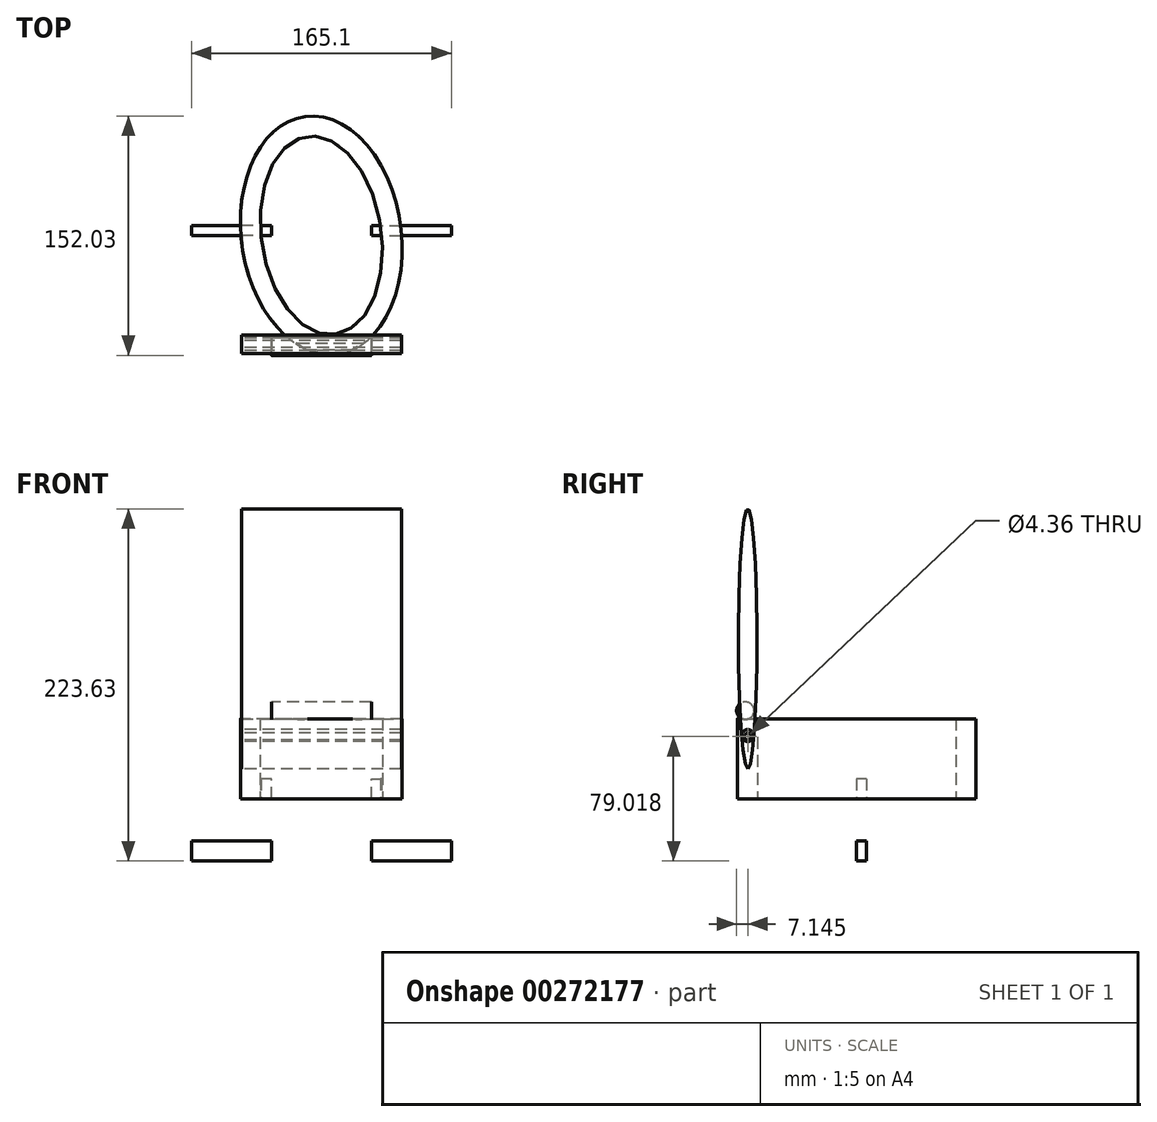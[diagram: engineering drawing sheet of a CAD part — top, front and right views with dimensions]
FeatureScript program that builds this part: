
annotation { "Feature Type Name" : "Feature", "Feature Type Description" : "" }
export const myFeature = defineFeature(function(context is Context, id is Id, definition is map)
    precondition{}
    {
        {
            var Q0;
            Q0=qCreatedBy(makeId("Top.planeOp"),FACE);
            var sketch = newSketch(context, id + "F0", { "sketchPlane" : qUnion([Q0])});
            skEllipse(sketch, "E0", {"center": v(0, 0) * mm, "majorRadius": 76.2 * mm, "minorRadius": 50.8 * mm, "majorAxis": v(-0.14, 1)});
            skEllipse(sketch, "E1", {"center": v(0, 0) * mm, "majorRadius": 63.5 * mm, "minorRadius": 38.1 * mm, "majorAxis": v(0.14, -0.99)});
            skSolve(sketch);
        }
        {
            var Q0;
            Q0 = qSketchRegion(id + "F0", true);
            extrude(context, id + "F1", {"entities" : qUnion([Q0]), "depth" : 50.8 * mm});
        }
        {
            var Q0;
            Q0=qCreatedBy(makeId("Right.planeOp"),FACE);
            var sketch = newSketch(context, id + "F2", { "sketchPlane" : qUnion([Q0])});
            skCircle(sketch, "E2", {"center": v(-70.68, 55.96) * mm, "radius": 5.55 * mm});
            skPoint(sketch, "E2.first.point", {"position": v(-69.37, 50.57) * mm});
            skPoint(sketch, "E2.second.point", {"position": v(-76.08, 57.27) * mm});
            skPoint(sketch, "E2.third.point", {"position": v(-65.58, 58.15) * mm});
            skSolve(sketch);
        }
        {
            var Q0;
            Q0 = qSketchRegion(id + "F2", true);
            extrude(context, id + "F3", {"entities" : qUnion([Q0]), "operationType" : NewBodyOperationType.ADD, "endBound" : BoundingType.SYMMETRIC, "depth" : 63.5 * mm});
        }
        {
            var Q0;
            Q0=qCreatedBy(makeId("Right.planeOp"),FACE);
            var sketch = newSketch(context, id + "F4", { "sketchPlane" : qUnion([Q0])});
            skLineSegment(sketch, "E3", {"start": v(-75.48, 50.8) * mm, "end": v(-75.48, 101.6) * mm});
            skLineSegment(sketch, "E4", {"start": v(-75.48, 101.6) * mm, "end": v(-69.13, 101.6) * mm});
            skEllipse(sketch, "E5", {"center": v(-69.13, 101.6) * mm, "majorRadius": 82.55 * mm, "minorRadius": 5.9 * mm, "majorAxis": v(0, -1)});
            skCircle(sketch, "E6", {"center": v(-69.09, 39.54) * mm, "radius": 2.18 * mm});
            skPoint(sketch, "E7", {"position": v(-66.83, 25.61) * mm});
            skPoint(sketch, "E8", {"position": v(-71.43, 25.61) * mm});
            skPoint(sketch, "E9", {"position": v(-69.09, 19.06) * mm});
            skPoint(sketch, "E10", {"position": v(-69.42, 66.59) * mm});
            skPoint(sketch, "E11", {"position": v(-69.42, 55.14) * mm});
            skPoint(sketch, "E12", {"position": v(-72.52, 34.04) * mm});
            skPoint(sketch, "E13", {"position": v(-76.14, 43.42) * mm});
            skPoint(sketch, "E14", {"position": v(-73.53, 46.73) * mm});
            skPoint(sketch, "E15", {"position": v(-79.04, 51.6) * mm});
            skPoint(sketch, "E16", {"position": v(-79.04, 59) * mm});
            skPoint(sketch, "E17", {"position": v(-93.58, 72.66) * mm});
            skPoint(sketch, "E18", {"position": v(-114.57, 57.23) * mm});
            skPoint(sketch, "E19", {"position": v(-122, 80.72) * mm});
            skPoint(sketch, "E20", {"position": v(-131.05, 64.73) * mm});
            skPoint(sketch, "E21", {"position": v(-91.64, 41.1) * mm});
            skPoint(sketch, "E22", {"position": v(-123.62, 70.9) * mm});
            skPoint(sketch, "E23", {"position": v(-112.64, 63.73) * mm});
            skPoint(sketch, "E24", {"position": v(-153.33, 104.96) * mm});
            skPoint(sketch, "E25", {"position": v(-150.43, 97.35) * mm});
            skPoint(sketch, "E26", {"position": v(-136.86, 74.16) * mm});
            skPoint(sketch, "E27", {"position": v(-157.53, 72.19) * mm});
            skPoint(sketch, "E28", {"position": v(-151.4, 80.3) * mm});
            skPoint(sketch, "E29", {"position": v(-137.83, 101.31) * mm});
            skPoint(sketch, "E30", {"position": v(-127.5, 102.11) * mm});
            skPoint(sketch, "E31", {"position": v(-121.03, 101.31) * mm});
            skPoint(sketch, "E32", {"position": v(70.57, 31.12) * mm});
            skPoint(sketch, "E33", {"position": v(15.34, 45.87) * mm});
            skPoint(sketch, "E34", {"position": v(-74.15, 58.32) * mm});
            skPoint(sketch, "E35", {"position": v(0, 43.25) * mm});
            skPoint(sketch, "E36", {"position": v(-42.76, 43.64) * mm});
            skPoint(sketch, "E37", {"position": v(-418.92, 103.4) * mm});
            skPoint(sketch, "E38", {"position": v(-285.67, 68.87) * mm});
            skPoint(sketch, "E39", {"position": v(-251.47, 61.32) * mm});
            skPoint(sketch, "E40", {"position": v(-242.55, 74.5) * mm});
            skPoint(sketch, "E41", {"position": v(-264.45, 85.57) * mm});
            skPoint(sketch, "E42", {"position": v(-318.16, 94.28) * mm});
            skPoint(sketch, "E43", {"position": v(-322.32, 66.51) * mm});
            skPoint(sketch, "E44", {"position": v(-345.2, 72.11) * mm});
            skPoint(sketch, "E45", {"position": v(-198, 67.1) * mm});
            skPoint(sketch, "E46", {"position": v(-192.57, 67.82) * mm});
            skPoint(sketch, "E47", {"position": v(-357.68, 99.84) * mm});
            skPoint(sketch, "E48", {"position": v(-133.05, 62.29) * mm});
            skPoint(sketch, "E49", {"position": v(-278.38, 99.55) * mm});
            skPoint(sketch, "E50", {"position": v(-320.86, 109.73) * mm});
            skPoint(sketch, "E51", {"position": v(-202.9, 81.87) * mm});
            skPoint(sketch, "E52", {"position": v(70.57, 26.67) * mm});
            skPoint(sketch, "E53", {"position": v(70.57, 42.77) * mm});
            skPoint(sketch, "E54", {"position": v(164.86, 27.95) * mm});
            skPoint(sketch, "E55", {"position": v(168, -7.01) * mm});
            skPoint(sketch, "E56", {"position": v(170.66, -7.47) * mm});
            skPoint(sketch, "E57", {"position": v(-64.64, 48.24) * mm});
            skPoint(sketch, "E58", {"position": v(281.43, -4.1) * mm});
            skPoint(sketch, "E59", {"position": v(120.86, 30.08) * mm});
            skPoint(sketch, "E60", {"position": v(280.31, 1.68) * mm});
            skPoint(sketch, "E61", {"position": v(300.18, -2.91) * mm});
            skPoint(sketch, "E62", {"position": v(250.08, 15.34) * mm});
            skPoint(sketch, "E63", {"position": v(271.38, 12.18) * mm});
            skPoint(sketch, "E64", {"position": v(321.3, -9.4) * mm});
            skPoint(sketch, "E65", {"position": v(100.72, 31.12) * mm});
            skPoint(sketch, "E66", {"position": v(-464.88, 118.2) * mm});
            skPoint(sketch, "E67", {"position": v(-449.77, 117.4) * mm});
            skPoint(sketch, "E68", {"position": v(-442.02, 113.21) * mm});
            skPoint(sketch, "E69", {"position": v(-451.42, 110.42) * mm});
            skPoint(sketch, "E70", {"position": v(-473.12, 106.89) * mm});
            skPoint(sketch, "E71", {"position": v(-464.79, 105.58) * mm});
            skPoint(sketch, "E72", {"position": v(-418.6, 101.77) * mm});
            skPoint(sketch, "E73", {"position": v(-443.94, 110.56) * mm});
            skPoint(sketch, "E74", {"position": v(-350.68, 65.25) * mm});
            skPoint(sketch, "E75", {"position": v(-462.84, 117.58) * mm});
            skPoint(sketch, "E76", {"position": v(-428.05, 116) * mm});
            skPoint(sketch, "E77", {"position": v(-420.1, 115.15) * mm});
            skPoint(sketch, "E78", {"position": v(321.3, -3.32) * mm});
            skPoint(sketch, "E79", {"position": v(313.25, -3.09) * mm});
            skPoint(sketch, "E80", {"position": v(-48.13, 53.98) * mm});
            skPoint(sketch, "E81", {"position": v(-40.22, 53.96) * mm});
            skPoint(sketch, "E82", {"position": v(-45.54, 54.06) * mm});
            skPoint(sketch, "E83", {"position": v(-48.98, 46.26) * mm});
            skPoint(sketch, "E84", {"position": v(-53.22, 52.4) * mm});
            skPoint(sketch, "E85", {"position": v(-53, 57.74) * mm});
            skPoint(sketch, "E86", {"position": v(-44.64, 45.7) * mm});
            skPoint(sketch, "E87", {"position": v(-47.4, 45.29) * mm});
            skPoint(sketch, "E88", {"position": v(-56.02, 49.19) * mm});
            skPoint(sketch, "E89", {"position": v(-46.53, 48.24) * mm});
            skPoint(sketch, "E90", {"position": v(-48.86, 52.44) * mm});
            skPoint(sketch, "E91", {"position": v(-47.14, 51.22) * mm});
            skPoint(sketch, "E92", {"position": v(-39.44, 38.32) * mm});
            skPoint(sketch, "E93", {"position": v(-39.79, 37.24) * mm});
            skPoint(sketch, "E94", {"position": v(-39.46, 36.47) * mm});
            skPoint(sketch, "E95", {"position": v(-33.97, 33.77) * mm});
            skPoint(sketch, "E96", {"position": v(-29.52, 31.12) * mm});
            skPoint(sketch, "E97", {"position": v(-29.52, 30.5) * mm});
            skPoint(sketch, "E98", {"position": v(-73.8, 51.22) * mm});
            skPoint(sketch, "E99", {"position": v(-74.9, 48.02) * mm});
            skPoint(sketch, "E100", {"position": v(-79.44, 43.43) * mm});
            skPoint(sketch, "E101", {"position": v(-102.27, 48.24) * mm});
            skPoint(sketch, "E102", {"position": v(-97.45, 48.24) * mm});
            skPoint(sketch, "E103", {"position": v(-64.26, 55.21) * mm});
            skSolve(sketch);
        }
        {
            var Q0;
            Q0 = qSketchRegion(id + "F4", true);
            extrude(context, id + "F5", {"entities" : qUnion([Q0]), "endBound" : BoundingType.SYMMETRIC, "depth" : 101.6 * mm});
        }
        {
            var Q0;
            Q0=qCreatedBy(makeId("Right.planeOp"),FACE);
            var sketch = newSketch(context, id + "F6", { "sketchPlane" : qUnion([Q0])});
            skCircle(sketch, "E104", {"center": v(-69.2, 40.2) * mm, "radius": 3.82 * mm});
            skSolve(sketch);
        }
        {
            var Q0;
            Q0 = qSketchRegion(id + "F6", true);
            extrude(context, id + "F7", {"entities" : qUnion([Q0]), "endBound" : BoundingType.SYMMETRIC, "depth" : 101.6 * mm});
        }
        {
            var Q0;
            Q0=qCreatedBy(makeId("Front.planeOp"),FACE);
            var sketch = newSketch(context, id + "F8", { "sketchPlane" : qUnion([Q0])});
            skLineSegment(sketch, "E105", {"start": v(0, 0) * mm, "end": v(-31.75, 0) * mm});
            skLineSegment(sketch, "E106", {"start": v(0, 0) * mm, "end": v(31.75, 0) * mm});
            skLineSegment(sketch, "E107.bottom", {"start": v(31.75, 0) * mm, "end": v(41.91, 0) * mm});
            skLineSegment(sketch, "E107.top", {"start": v(31.75, 12.7) * mm, "end": v(41.91, 12.7) * mm});
            skLineSegment(sketch, "E107.left", {"start": v(31.75, 0) * mm, "end": v(31.75, 12.7) * mm});
            skLineSegment(sketch, "E107.right", {"start": v(41.91, 0) * mm, "end": v(41.91, 12.7) * mm});
            skLineSegment(sketch, "E108.bottom", {"start": v(-31.75, 0) * mm, "end": v(-41.91, 0) * mm});
            skLineSegment(sketch, "E108.top", {"start": v(-31.75, 12.7) * mm, "end": v(-41.91, 12.7) * mm});
            skLineSegment(sketch, "E108.left", {"start": v(-31.75, 0) * mm, "end": v(-31.75, 12.7) * mm});
            skLineSegment(sketch, "E108.right", {"start": v(-41.91, 0) * mm, "end": v(-41.91, 12.7) * mm});
            skSolve(sketch);
        }
        {
            var Q0;
            Q0 = qSketchRegion(id + "F8", true);
            extrude(context, id + "F9", {"entities" : qUnion([Q0]), "operationType" : NewBodyOperationType.ADD, "oppositeDirection" : true, "depth" : 6.35 * mm});
        }
        {
            var Q0;
            Q0=qCreatedBy(makeId("Front.planeOp"),FACE);
            var sketch = newSketch(context, id + "F10", { "sketchPlane" : qUnion([Q0])});
            skLineSegment(sketch, "E109", {"start": v(0, -39.48) * mm, "end": v(31.75, -39.48) * mm});
            skLineSegment(sketch, "E110", {"start": v(0, -39.48) * mm, "end": v(-31.75, -39.48) * mm});
            skLineSegment(sketch, "E111.bottom", {"start": v(-31.75, -39.48) * mm, "end": v(-82.55, -39.48) * mm});
            skLineSegment(sketch, "E111.top", {"start": v(-31.75, -26.78) * mm, "end": v(-82.55, -26.78) * mm});
            skLineSegment(sketch, "E111.left", {"start": v(-31.75, -39.48) * mm, "end": v(-31.75, -26.78) * mm});
            skLineSegment(sketch, "E111.right", {"start": v(-82.55, -39.48) * mm, "end": v(-82.55, -26.78) * mm});
            skLineSegment(sketch, "E112.bottom", {"start": v(31.75, -39.48) * mm, "end": v(82.55, -39.48) * mm});
            skLineSegment(sketch, "E112.top", {"start": v(31.75, -26.78) * mm, "end": v(82.55, -26.78) * mm});
            skLineSegment(sketch, "E112.left", {"start": v(31.75, -39.48) * mm, "end": v(31.75, -26.78) * mm});
            skLineSegment(sketch, "E112.right", {"start": v(82.55, -39.48) * mm, "end": v(82.55, -26.78) * mm});
            skSolve(sketch);
        }
        {
            var Q0;
            Q0 = qSketchRegion(id + "F10", true);
            extrude(context, id + "F11", {"entities" : qUnion([Q0]), "oppositeDirection" : true, "depth" : 6.35 * mm});
        }
    });
